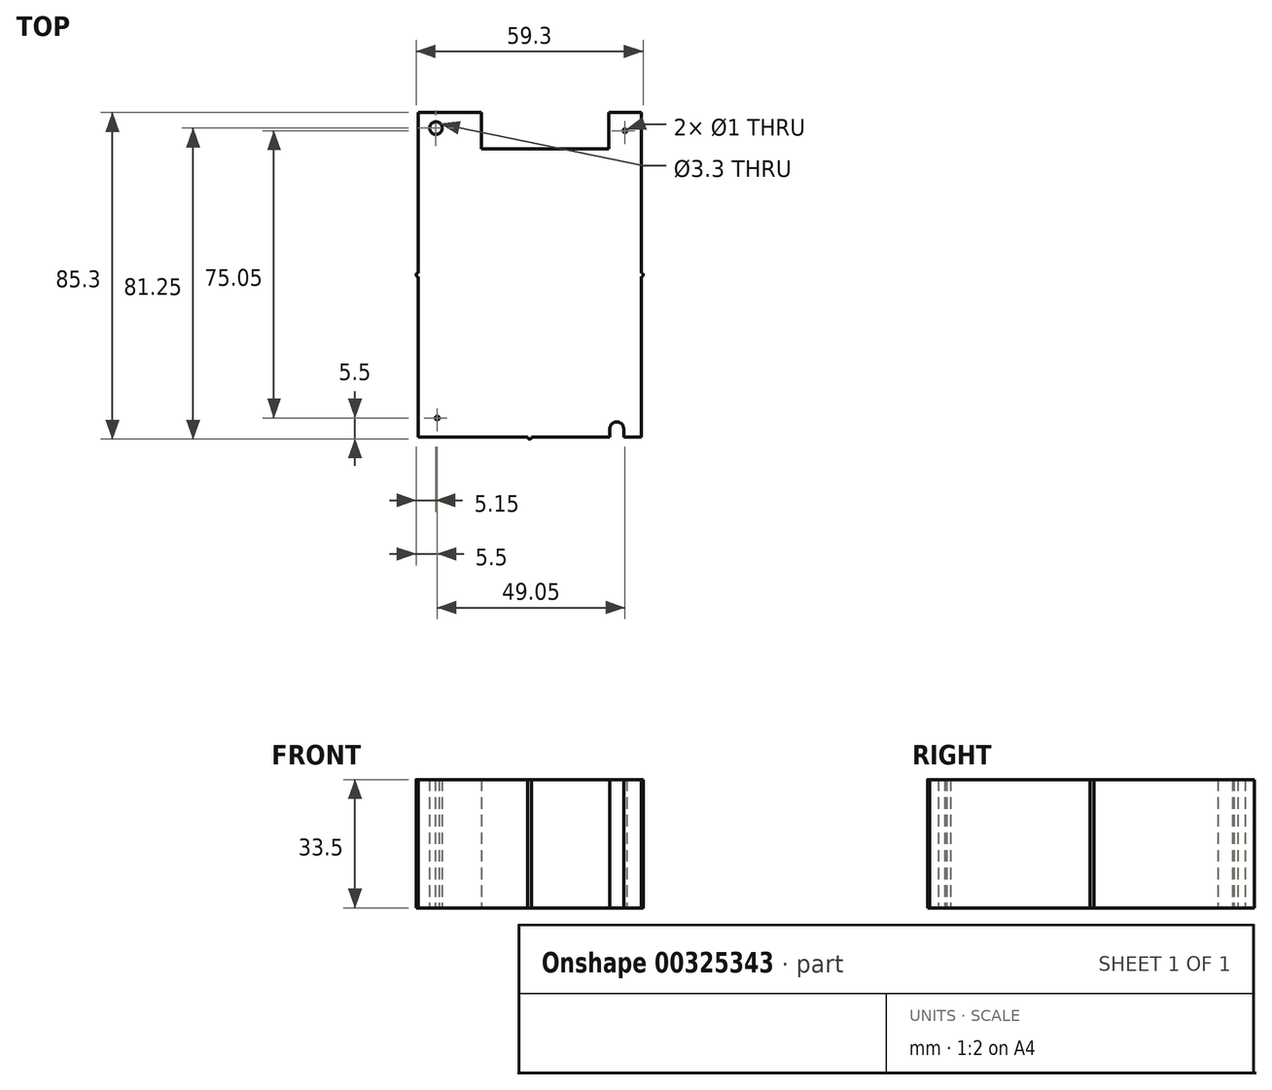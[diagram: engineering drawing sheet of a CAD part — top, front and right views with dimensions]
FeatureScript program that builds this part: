
annotation { "Feature Type Name" : "Feature", "Feature Type Description" : "" }
export const myFeature = defineFeature(function(context is Context, id is Id, definition is map)
    precondition{}
    {
        {
            var Q0;
            Q0=qCreatedBy(makeId("Top.planeOp"),FACE);
            var sketch = newSketch(context, id + "F0", { "sketchPlane" : qUnion([Q0])});
            skLineSegment(sketch, "E0.bottom", {"start": v(-29.15, 42.4) * mm, "end": v(-12.55, 42.4) * mm});
            skLineSegment(sketch, "E0.top", {"start": v(-29.15, -42.4) * mm, "end": v(20.95, -42.4) * mm});
            skLineSegment(sketch, "E0.left", {"start": v(-29.15, 42.4) * mm, "end": v(-29.15, -42.4) * mm});
            skLineSegment(sketch, "E0.right", {"start": v(29.15, 42.4) * mm, "end": v(29.15, -42.4) * mm});
            skCircle(sketch, "E1", {"center": v(-24.5, 38.35) * mm, "radius": 1.65 * mm});
            skArc(sketch, "E2", {"start": v(24.55, -40.1) * mm, "mid": v(22.75, -38.4) * mm, "end": v(20.95, -40.1) * mm});
            skLineSegment(sketch, "E3", {"start": v(-12.55, 32.9) * mm, "end": v(20.65, 32.9) * mm});
            skLineSegment(sketch, "E4", {"start": v(20.65, 32.9) * mm, "end": v(20.65, 42.4) * mm});
            skLineSegment(sketch, "E5", {"start": v(-12.55, 32.9) * mm, "end": v(-12.55, 42.4) * mm});
            skLineSegment(sketch, "E6.trimOffspring", {"start": v(20.65, 42.4) * mm, "end": v(29.15, 42.4) * mm});
            skLineSegment(sketch, "E7", {"start": v(20.95, -40.1) * mm, "end": v(20.95, -42.4) * mm});
            skLineSegment(sketch, "E8.trimOffspring", {"start": v(24.55, -42.4) * mm, "end": v(29.15, -42.4) * mm});
            skLineSegment(sketch, "E9", {"start": v(24.55, -40.1) * mm, "end": v(24.55, -42.4) * mm});
            skCircle(sketch, "E10", {"center": v(0, -42.4) * mm, "radius": 0.5 * mm});
            skCircle(sketch, "E11", {"center": v(29.15, 0) * mm, "radius": 0.5 * mm});
            skCircle(sketch, "E12", {"center": v(-29.15, 0) * mm, "radius": 0.5 * mm});
            skLineSegment(sketch, "E13.left", {"start": v(-12.55, 42.4) * mm, "end": v(-12.55, 42.25) * mm});
            skCircle(sketch, "E14", {"center": v(24.9, 37.65) * mm, "radius": 0.5 * mm});
            skPoint(sketch, "E14.centerSnap0", {"position": v(20.65, 37.65) * mm});
            skPoint(sketch, "E14.centerSnap1", {"position": v(24.9, 42.4) * mm});
            skCircle(sketch, "E15", {"center": v(-24.15, -37.4) * mm, "radius": 0.5 * mm});
            skSolve(sketch);
        }
        {
            var Q0;
            Q0=qSketchRegion(id+"F0",true);
            extrude(context, id + "F1", {"entities" : qUnion([Q0]), "depth" : 33.5 * mm});
        }
    });
